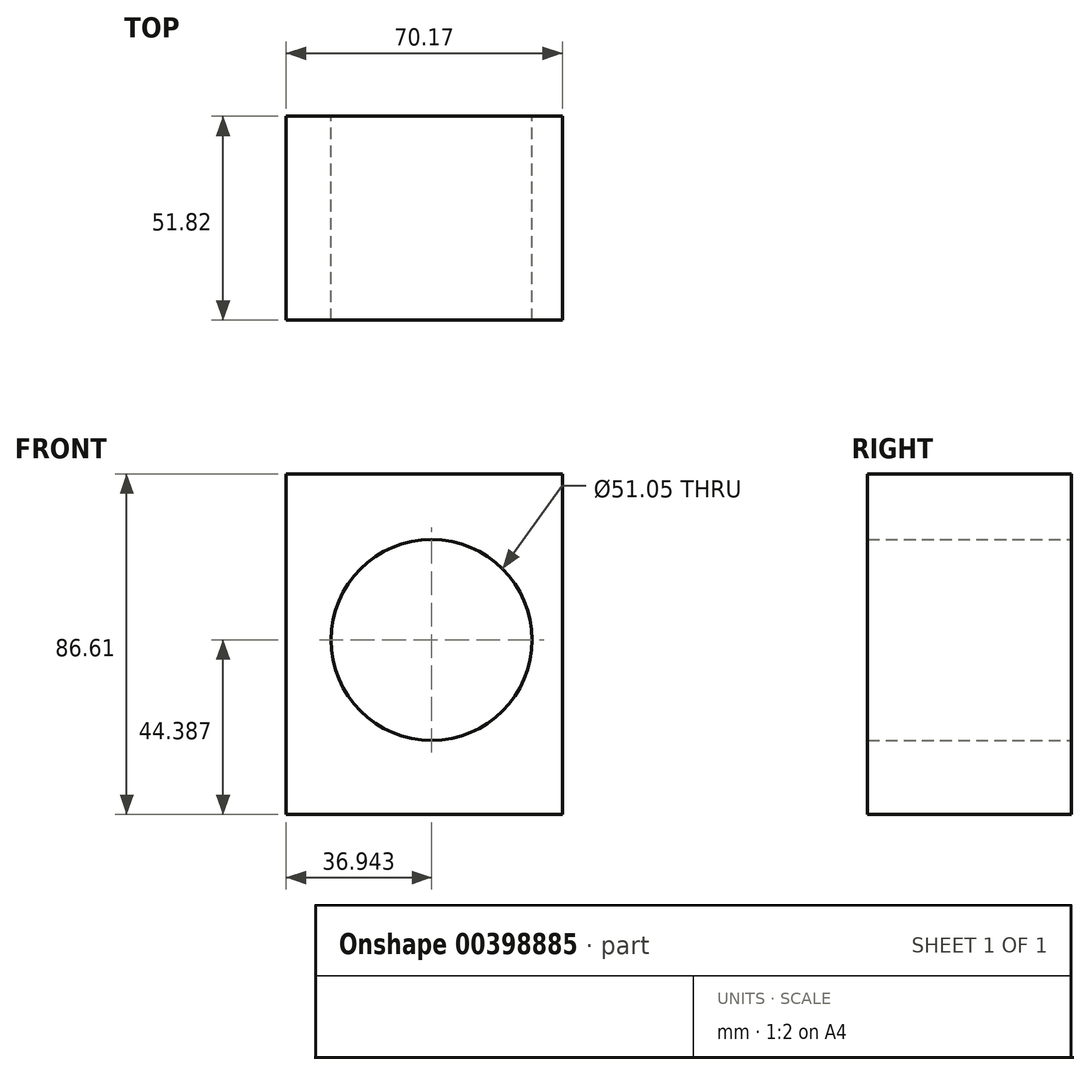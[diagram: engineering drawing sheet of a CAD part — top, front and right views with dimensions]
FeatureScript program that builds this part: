
annotation { "Feature Type Name" : "Feature", "Feature Type Description" : "" }
export const myFeature = defineFeature(function(context is Context, id is Id, definition is map)
    precondition{}
    {
        {
            var Q0;
            Q0=qCreatedBy(makeId("Front.planeOp"),FACE);
            var sketch = newSketch(context, id + "F0", { "sketchPlane" : qUnion([Q0])});
            skLineSegment(sketch, "E0.bottom", {"start": v(-52.02, 10.56) * mm, "end": v(18.15, 10.56) * mm});
            skLineSegment(sketch, "E0.top", {"start": v(-52.02, -76.05) * mm, "end": v(18.15, -76.05) * mm});
            skLineSegment(sketch, "E0.left", {"start": v(-52.02, 10.56) * mm, "end": v(-52.02, -76.05) * mm});
            skLineSegment(sketch, "E0.right", {"start": v(18.15, 10.56) * mm, "end": v(18.15, -76.05) * mm});
            skCircle(sketch, "E1", {"center": v(-15.08, -31.66) * mm, "radius": 25.52 * mm});
            skSolve(sketch);
        }
        {
            var Q0;
            Q0 = qSketchRegion(id + "F0", true);
            extrude(context, id + "F1", {"entities" : qUnion([Q0]), "depth" : 51.82 * mm});
        }
    });
